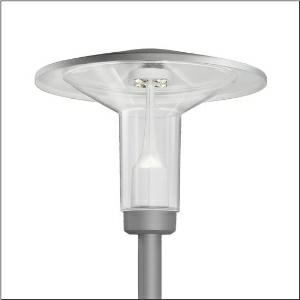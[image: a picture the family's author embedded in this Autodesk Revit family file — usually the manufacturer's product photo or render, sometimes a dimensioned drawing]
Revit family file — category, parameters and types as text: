
# Revit family: laterne_iq___st1_2a_5xa5255ef14h_6af0
name_source: partatom
category: Lighting Fixtures
units: mm (PartAtom-declared; Revit-internal decimal feet)

## family parameters
Cut with Voids When Loaded = No
Host = Face
Light Source = No
Part Type = Normal
Room Calculation Point = No
Round Connector Dimension = Use Diameter
Shared = No

## types (1)
- --- (1 x LED, 1540 lm, 10.5 W, 3000K)
    Apparent Load = 11 VA
    CIE Flux Codes = 25 63 94 98 100
    Color Rendering = 70
    Color Temperature = 3000K
    Default Elevation = 1800 mm
    Description = Lantern iQ, mast luminaire, Module 540 iQ-SR, primary light control with 3 zone facetted reflector, of plastic, silver coated, highly specular, structured, primary optical cover: cover, of PMMA, transparent, light distribution: ST1.2a, light emission: direct distribution, primary light characteristic: asymmetric, installation type: post-top, LED, High Power LED, rated luminous flux: 1.540lm, luminous efficacy: 147lm/W, light colour: 730, colour temperature: 3000K, control gear: iQ Street-Remote, control: Auto-Match, Temp-Guard, Lumen-Switch, Night-Set, Smart-Wire, Light-Fading, Desk-Remote (wireless, voltage-free reading and setting of iQ features in the workshop via application-optimized NFC function/RFID function), optimised constant luminous flux control (CLO 2.0), Street-Remote, pre-setting: logarithmic dimming characteristic, with terminal, 6-pole, max. 2.5mm², mains connection: 230..240V, AC, 50/60Hz, start of lifetime: 11W, end of service life: 11W, reduction: 5W, luminaire housing, upper part, of glass-fibre reinforced polyester, coated, Siteco® metallic grey (DB 702S), diameter: 750mm, height: 583mm, spigot size: d x l = 76 x 70mm (post-top) | with reducer (optional accessory) 60 x 70mm, mounting height: 3..5m, post-top mast mounting element, of diecast aluminium, coated, Siteco® metallic grey (DB 702S), Module 540 iQ-SR, traffic white (RAL 9016), equipment: standard, protection rating (complete): IP65, insulation class (complete): insulation class II (safety insulation), certification: CE, ENEC, VDE, packaging unit: 1 piece

Light Distribution: ST1.2a
    Height = 583 mm
    Lamp = 1 x LED
    Lamp Light Flux = 1540 lm
    Lamp Power = 10.5 W
    Lamp count = 1
    Length = 750 mm
    Luminous efficacy = 147 lm/W
    Manufacturer = Siteco
    ModVariant = No
    Model = 5XA5255EF14H
    Number of Poles = 1
    OnlyDefault = Yes
    Power Factor = 1
    Product Name = Laterne iQ | ST1.2a
    Product group = mast luminaire | pylon top
    ProductGroupID = 6100
    Protection Class = Protection class II
    Protection Degree = IP 65
    RLX_Detail_Level = 1
    RLX_Emergency_Light_Flux = 0 lm
    RLX_Emergency_Type = 0
    RLX_Emergency_Type_DB = No
    RlxData = <blob elided: 103553 chars, md5=a2febc31>
    Socket = socket
    Standby Power = 0 W
    System Light Flux = 1540 lm
    System Power = 11 W
    Type Comments = factory setting: luminous flux: 100 % | dim-lin: 254 | 419 mA
    Type Image = l_1006050.jpg
    URL = http://relux.com
    VarID = @adj_160113
    Voltage = 0 V
    Weight = 0.00 kg
    Width = 0 mm  [stored 0 ft]

note: [stored X ft] marks values corroborated as IEEE doubles in the binary element streams (Revit-internal decimal feet)

## geometry (parser evidence)
native form markers: Blend x4, Sweep x8
no freeform markers — native parametric forms only
